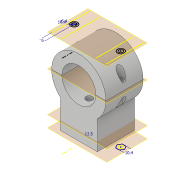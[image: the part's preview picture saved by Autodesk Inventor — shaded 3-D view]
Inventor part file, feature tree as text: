
AUTODESK INVENTOR PART (.ipt)
format: ipt  version: 2021 (Build 250183000, 183)  size: 211,456 bytes
history: native  units: mm
features: other x7, extrude x5, split x2, sketch x2, hole x1, imported_body x1
ambient origin geometry x8: Origin, YZ Plane, XZ Plane, XY Plane, X Axis, Y Axis, Z Axis, Center Point
bodies: Solid1 (feature_tree)
feature tree (18):
  extrude  "Extrusion1"  Depth=85.0mm
  other  "BoltPlane"
  other  "BoltHoles"
  extrude  "Extrusion2"  Depth=62.0mm
  extrude  "Extrusion3"  Depth=62.0mm TaperAngle=0.0deg
  other  "NutPlane"
  other  "NutHoles"
  extrude  "Extrusion4"  Depth=62.0mm
  other  "SplitPlane"
  split  "Split2"
  hole  "Hole2"  [1 undecoded]
  sketch  "Sketch4"  dims[d2=75.866mm d3=29.0mm d4=58.0mm d5=0.0mm d6=50.0mm d7=6.0mm d8=6.4mm d9=10.4mm d10=58.0mm d11=0.0mm d12=40.0mm d13=0.0mm d14=-80.0mm d15=10.4mm d16=70.0mm d17=0.0mm d18=0.0mm d28=12.5mm d29=6.2mm d30=6.0mm d31=4.0mm d32=2.0mm d33=90.0deg d34=8.0mm d35=0.0mm d36=10.2mm d37=10.2mm d38=18.0mm d39=62.0mm d40=0.0mm]
  other  "BoltHeadLevel"
  extrude  "Extrusion5"  Depth=62.0mm
  split  "Split3"
  sketch  "Sketch1"  dims[d0=53.0mm d1=85.0mm]
  other  "UPPER"
  imported_body  "BASE"
note: 1 required parameter value undecoded (feature->parameter linkage not recoverable at this tier; creation-order binding heuristic only, values carry confidence <= 0.55)
